# Revit family: BL716LEDHT
name_source: partatom
category: Lighting Fixtures
units: mm (PartAtom-declared; Revit-internal decimal feet)

## family parameters
Cut with Voids When Loaded = No
Host = Face
Light Source = Yes
Maintain Annotation Orientation = No
Part Type = Normal
Room Calculation Point = No
Round Connector Dimension = Use Diameter
Shared = No

## types (3) — shared parameters
Color Filter = 16777215
Default Elevation = 4' - 0"
Dimming Lamp Color Temperature Shift = <None>
Emit from Line Length = 2' - 0"
HOUSING MATERIAL = HOUSING MATERIAL
LENS MATERIAL = LENS MATERIAL
Lamp = LED
Manufacturer = BEGHELLI
Model = BL716LED
Tilt Angle = -90.00°
Type Image = BL716LED.PNG

## per-type parameters (varying)
| type | Photometric Web File | Wattage Comments |
| BL726LEDHTHOWT40120-277V | BL716LEDHTHOWT40120-277 TO REVIT.ies | 40W |
| BL726LEDHTLOWT40120-277V | BL716LEDHTLOWT40120-277 TO REVIT.ies | 20W |
| BL726LEDHTMOWT40120-277V | BL716LEDHTMOWT40120-277 TO REVIT.ies | 30W |

## geometry (parser evidence)
native form markers: Sweep x20
no freeform markers — native parametric forms only
